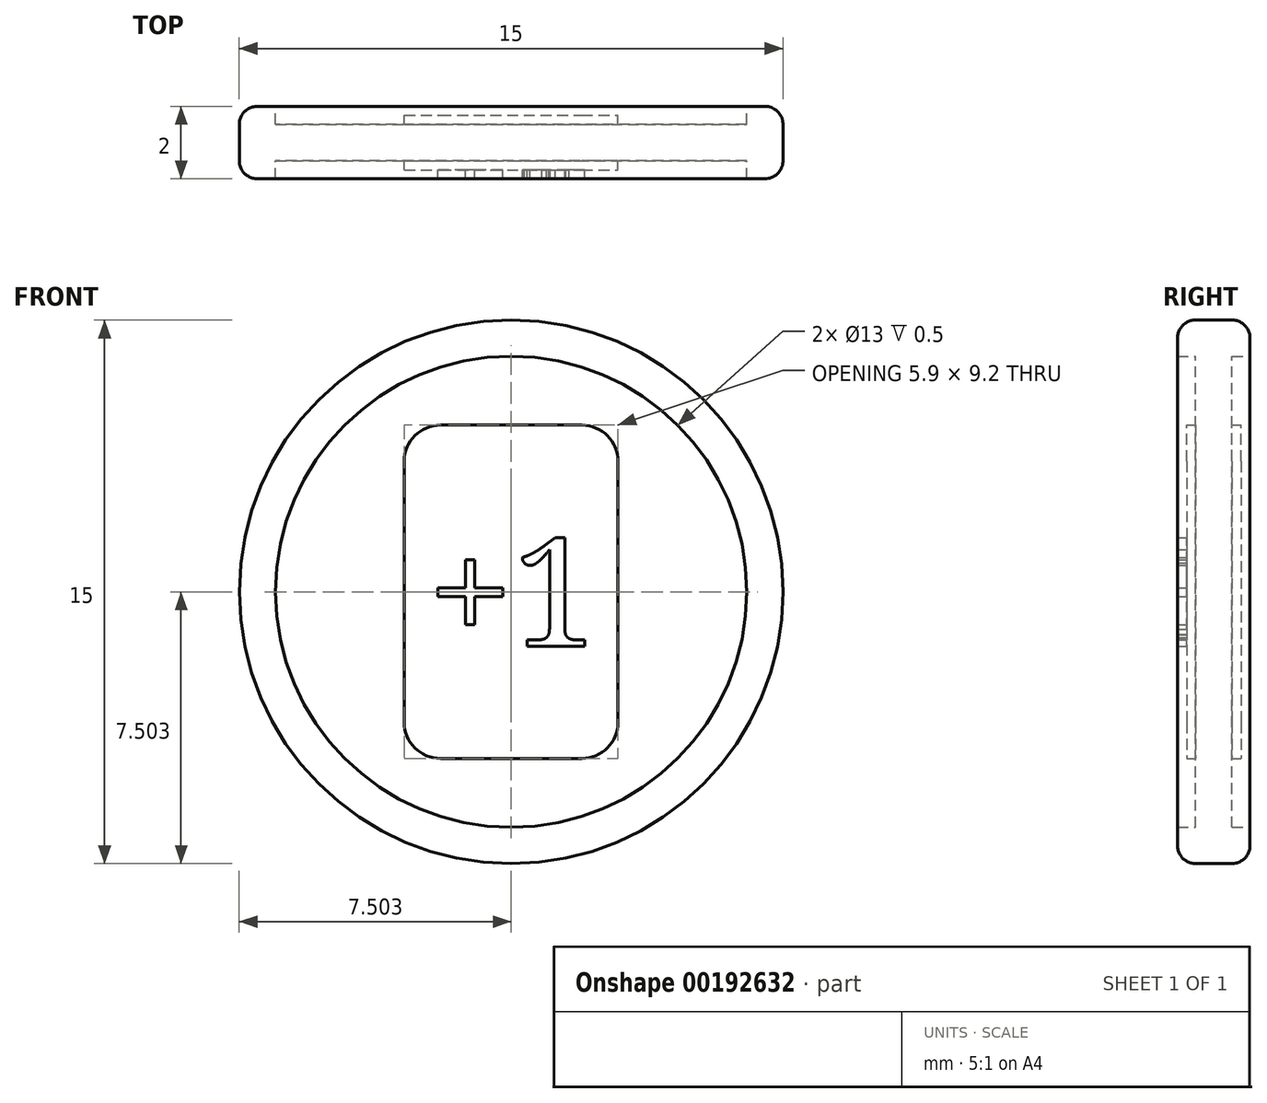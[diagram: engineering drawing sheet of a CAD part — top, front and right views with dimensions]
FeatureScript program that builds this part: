
annotation { "Feature Type Name" : "Feature", "Feature Type Description" : "" }
export const myFeature = defineFeature(function(context is Context, id is Id, definition is map)
    precondition{}
    {
        {
            var Q0;
            Q0=qCreatedBy(makeId("Front.planeOp"),FACE);
            var sketch = newSketch(context, id + "F0", { "sketchPlane" : qUnion([Q0])});
            skLineSegment(sketch, "E0.bottom", {"start": v(19.61, 29.82) * mm, "end": v(23.51, 29.82) * mm});
            skLineSegment(sketch, "E0.top", {"start": v(19.61, 20.62) * mm, "end": v(23.51, 20.62) * mm});
            skLineSegment(sketch, "E0.left", {"start": v(18.61, 28.82) * mm, "end": v(18.61, 21.62) * mm});
            skLineSegment(sketch, "E0.right", {"start": v(24.51, 28.82) * mm, "end": v(24.51, 21.62) * mm});
            skText(sketch, "E1", { "text": "+1", "fontName": "NotoSerif-Regular.ttf"});
            skPoint(sketch, "E2", {"position": v(21.56, 25.22) * mm});
            skLineSegment(sketch, "E3", {"start": v(18.61, 25.22) * mm, "end": v(24.51, 25.22) * mm, "construction": true});
            skCircle(sketch, "E4", {"center": v(21.56, 25.22) * mm, "radius": 7.5 * mm});
            skCircle(sketch, "E5", {"center": v(21.56, 25.22) * mm, "radius": 6.5 * mm});
            skPoint(sketch, "E6.visualSharp", {"position": v(18.61, 29.82) * mm});
            skArc(sketch, "E6.filletArc", {"start": v(19.61, 29.82) * mm, "mid": v(18.9, 29.53) * mm, "end": v(18.61, 28.82) * mm});
            skPoint(sketch, "E7.visualSharp", {"position": v(18.61, 20.62) * mm});
            skArc(sketch, "E7.filletArc", {"start": v(18.61, 21.62) * mm, "mid": v(18.9, 20.92) * mm, "end": v(19.61, 20.62) * mm});
            skPoint(sketch, "E8.visualSharp", {"position": v(24.51, 20.62) * mm});
            skArc(sketch, "E8.filletArc", {"start": v(23.51, 20.62) * mm, "mid": v(24.22, 20.92) * mm, "end": v(24.51, 21.62) * mm});
            skPoint(sketch, "E9.visualSharp", {"position": v(24.51, 29.82) * mm});
            skArc(sketch, "E9.filletArc", {"start": v(24.51, 28.82) * mm, "mid": v(24.22, 29.53) * mm, "end": v(23.51, 29.82) * mm});
            const initialGuessF0  = {"E1": [0.01927, 0.02372, 1, 0, 0.003]};
            skSetInitialGuess(sketch, initialGuessF0);
            skSolve(sketch);
        }
        {
            var Q0;
            Q0=makeQuery(id+"F0.imprint","IMPRINT",FACE,{"disambiguationData":[TD([[makeQuery(id+"F0.imprint","IMPRINT",EDGE,{"derivedFrom":sQuery(id+"F0.wireOp",EDGE,"E0.bottom")}),1.0]])]});
            extrude(context, id + "F1", {"entities" : qUnion([Q0]), "endBound" : BoundingType.SYMMETRIC, "depth" : 1 * mm});
        }
        {
            var Q0;
            Q0=makeQuery(id+"F0.imprint","IMPRINT",FACE,{"disambiguationData":[TD([[makeQuery(id+"F0.imprint","IMPRINT",EDGE,{"derivedFrom":sQuery(id+"F0.wireOp",EDGE,"E0.bottom")}),-1.0]])]});
            extrude(context, id + "F2", {"entities" : qUnion([Q0]), "operationType" : NewBodyOperationType.ADD, "endBound" : BoundingType.SYMMETRIC, "depth" : 1.5 * mm});
        }
        {
            var Q0;
            Q0=makeQuery(id+"F0.imprint","IMPRINT",FACE,{"disambiguationData":[TD([[makeQuery(id+"F0.imprint","IMPRINT",EDGE,{"derivedFrom":sQuery(id+"F0.wireOp",EDGE,"E4")}),1.0]])]});
            extrude(context, id + "F3", {"entities" : qUnion([Q0]), "operationType" : NewBodyOperationType.ADD, "endBound" : BoundingType.SYMMETRIC, "depth" : 2 * mm});
        }
        {
            var Q0;
            Q0=makeQuery(id+"F3.opExtrude","CAP_EDGE",EDGE,{"disambiguationData":[OSD([sQuery(id+"F0.wireOp",EDGE,"E4")])],"isStart":false});
            var Q1;
            Q1=makeQuery(id+"F3.opExtrude","CAP_EDGE",EDGE,{"disambiguationData":[OSD([sQuery(id+"F0.wireOp",EDGE,"E4")])],"isStart":true});
            fillet(context, id + "F4", {"entities" : qUnion([Q0, Q1]), "radius" : 0.5 * mm, "tangentPropagation" : true, "allowEdgeOverflow" : false});
        }
        {
            var Q0;
            Q0=makeQuery(id+"F0.imprint","IMPRINT",FACE,{"disambiguationData":[TD([[makeQuery(id+"F0.imprint","IMPRINT",EDGE,{"derivedFrom":sQuery(id+"F0.wireOp",EDGE,"E1.sketch_text.stroke-0")}),-1.0]])]});
            var Q1;
            Q1=makeQuery(id+"F0.imprint","IMPRINT",FACE,{"disambiguationData":[TD([[makeQuery(id+"F0.imprint","IMPRINT",EDGE,{"derivedFrom":sQuery(id+"F0.wireOp",EDGE,"E1.sketch_text.stroke-12")}),-1.0]])]});
            extrude(context, id + "F5", {"entities" : qUnion([Q0, Q1]), "operationType" : NewBodyOperationType.ADD, "depth" : 1 * mm});
        }
        {
            var Q0;
            Q0=makeQuery(id+"F0.imprint","IMPRINT",FACE,{"disambiguationData":[TD([[makeQuery(id+"F0.imprint","IMPRINT",EDGE,{"derivedFrom":sQuery(id+"F0.wireOp",EDGE,"E1.sketch_text.stroke-12")}),-1.0]])]});
            var Q1;
            Q1=makeQuery(id+"F0.imprint","IMPRINT",FACE,{"disambiguationData":[TD([[makeQuery(id+"F0.imprint","IMPRINT",EDGE,{"derivedFrom":sQuery(id+"F0.wireOp",EDGE,"E1.sketch_text.stroke-0")}),-1.0]])]});
            extrude(context, id + "F6", {"entities" : qUnion([Q0, Q1]), "operationType" : NewBodyOperationType.ADD, "oppositeDirection" : true, "depth" : 1.5 / 2 * mm});
        }
    });
